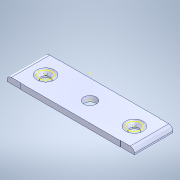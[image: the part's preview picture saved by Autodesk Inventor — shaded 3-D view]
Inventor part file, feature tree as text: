
AUTODESK INVENTOR PART (.ipt)
format: ipt  version: 2021 (Build 250183000, 183)  size: 254,976 bytes
history: mixed  units: in
note: dims shown in document units (in); Inventor stores cm internally (conversion verified against a paired STEP export)
features: sketch x12, extrude x7, hole x2, reference x2, other x2, fillet x1, projected_geometry x1, mirror x1, imported_body x1
ambient origin geometry x8: Origin, YZ Plane, XZ Plane, XY Plane, X Axis, Y Axis, Z Axis, Center Point
bodies: Solid1 (imported_parasolid)
feature tree (29):
  extrude  "Extrusion1"  Depth=0.0039in
  sketch  "Sketch2"  dims[d3=0.1339in d4=0.2362in d5=0.248in d6=0.0787in d7=90.0deg d8=0.315in d9=0.0in d14=0.0039in]
  hole  "Hole1"  [1 undecoded]
  sketch  "Sketch4"  dims[d17=0.3937in d18=0.0in d20=0.5472in]
  extrude  "Extrusion3"  Depth=0.5472in
  extrude  "Extrusion4"  Depth=0.3937in TaperAngle=0.0deg
  fillet  "Fillet3"  Radius=0.0591in
  extrude  "Extrusion5"  Depth=0.3937in TaperAngle=0.0deg
  extrude  "Extrusion6"  Depth=0.4921in
  extrude  "Extrusion7"  Depth=0.4803in
  extrude  "Extrusion8"  Depth=0.315in
  sketch  "Sketch12"
  hole  "Hole2"  [1 undecoded]
  sketch  "Sketch1"  dims[d0=0.3937in d1=0.0in]
  reference  "Reference1"
  reference  "Reference2"
  sketch  "Sketch3"  dims[d15=1.8071in d16=0.5551in]
  sketch  "Sketch6"  dims[d21=0.1969in d22=0.3937in d23=0.0in d24=0.0591in]
  sketch  "Sketch7"  dims[d25=0.3937in d26=0.0in d27=0.3937in d28=0.0in]
  sketch  "Sketch8"  dims[d29=0.5709in d30=0.4921in]
  projected_geometry  "Projected Loop2"
  sketch  "Sketch9"  dims[d31=0.3937in d32=0.0in d33=0.4803in]
  sketch  "Sketch10"  dims[d34=0.315in d35=0.0in d36=0.3543in]
  sketch  "Sketch11"  dims[d37=0.0709in d38=0.2362in d39=0.1417in d40=0.0787in d41=90.0deg d42=0.315in d43=0.0in]
  sketch  "Sketch13"
  mirror  "Mirror1"
  other  "assy_gic_kinematic_2d_robot_arm_MK1_v2.iam"
  other  "base_bearing_holder_v1:1"
  imported_body  NMx_Import_Brep_tag  [imported B-rep: ~38 faces, bbox_mm=[45.9, 10.0, 14.5]]
note: 2 required parameter values undecoded (feature->parameter linkage not recoverable at this tier; creation-order binding heuristic only, values carry confidence <= 0.55)
